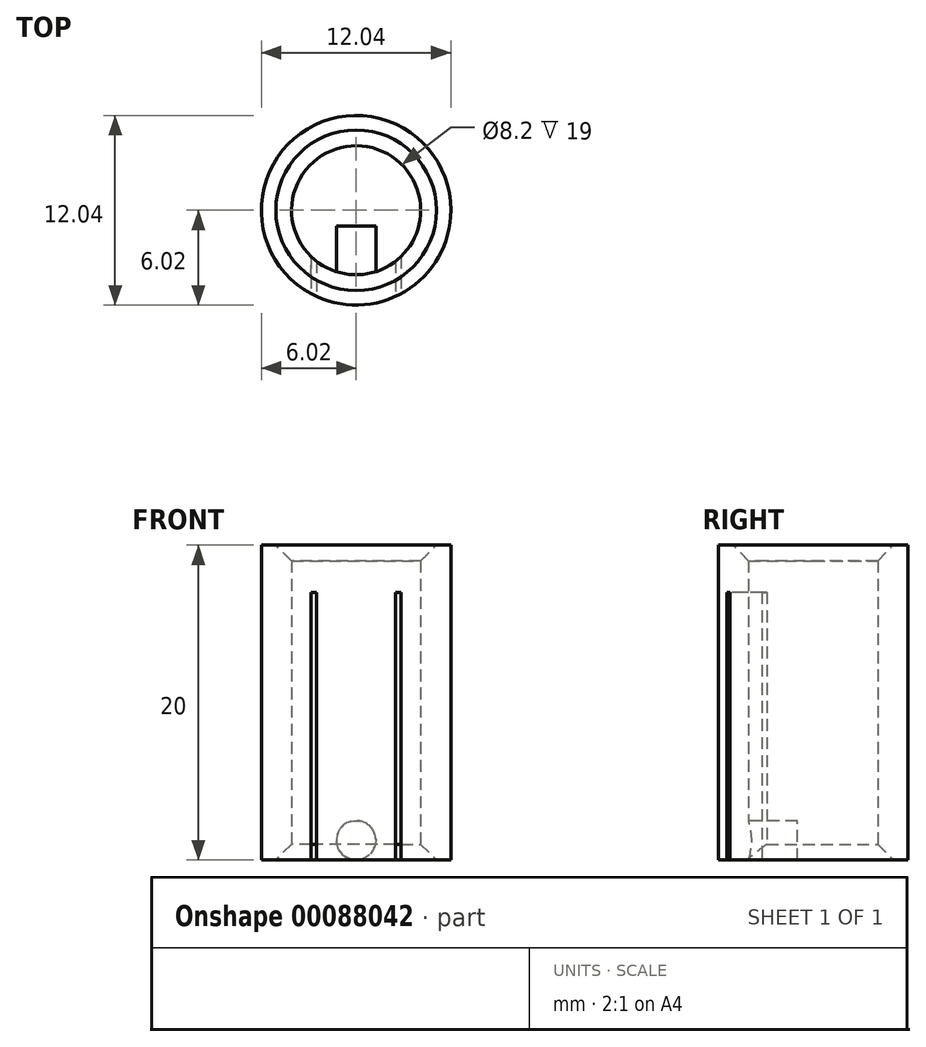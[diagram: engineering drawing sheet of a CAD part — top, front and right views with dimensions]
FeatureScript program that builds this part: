
annotation { "Feature Type Name" : "Feature", "Feature Type Description" : "" }
export const myFeature = defineFeature(function(context is Context, id is Id, definition is map)
    precondition{}
    {
        {
            var Q0;
            Q0=qCreatedBy(makeId("Top.planeOp"),FACE);
            var sketch = newSketch(context, id + "F0", { "sketchPlane" : qUnion([Q0])});
            skCircle(sketch, "E0", {"center": v(0, 0) * mm, "radius": 4.1 * mm});
            skCircle(sketch, "E1", {"center": v(0, 0) * mm, "radius": 6.02 * mm});
            skSolve(sketch);
        }
        {
            var Q0;
            Q0=makeQuery(id+"F0.imprint","IMPRINT",FACE,{"disambiguationData":[TD([[makeQuery(id+"F0.imprint","IMPRINT",EDGE,{"derivedFrom":sQuery(id+"F0.wireOp",EDGE,"E0")}),-1.0]])]});
            extrude(context, id + "F1", {"entities" : qUnion([Q0]), "depth" : 20 * mm});
        }
        {
            var Q0;
            Q0=qCreatedBy(makeId("Front.planeOp"),FACE);
            cPlane(context, id + "F2", {"entities" : qUnion([Q0]), "cplaneType" : CPlaneType.OFFSET, "offset" : 5 * mm, "width" : 150 * mm, "height" : 150 * mm});
        }
        {
            var Q0;
            Q0=qCreatedBy(id+"F2.planeOp",FACE);
            var sketch = newSketch(context, id + "F3", { "sketchPlane" : qUnion([Q0])});
            skCircle(sketch, "E2", {"center": v(0, 1.25) * mm, "radius": 1.25 * mm});
            skSolve(sketch);
        }
        {
            var Q0;
            Q0 = qSketchRegion(id + "F3", true);
            extrude(context, id + "F4", {"entities" : qUnion([Q0]), "operationType" : NewBodyOperationType.ADD, "oppositeDirection" : true, "depth" : 4 * mm});
        }
        {
            var Q0;
            Q0=qCreatedBy(id+"F2.planeOp",FACE);
            var sketch = newSketch(context, id + "F5", { "sketchPlane" : qUnion([Q0])});
            skLineSegment(sketch, "E3", {"start": v(-2.85, 0) * mm, "end": v(-2.85, 17) * mm});
            skLineSegment(sketch, "E4.0", {"start": v(-2.5, 0) * mm, "end": v(-2.5, 17) * mm});
            skLineSegment(sketch, "E5", {"start": v(-2.85, 17) * mm, "end": v(-2.5, 17) * mm});
            skLineSegment(sketch, "E6", {"start": v(-2.5, 0) * mm, "end": v(-2.85, 0) * mm});
            skLineSegment(sketch, "E7.MirrorCS", {"start": v(2.5, 0) * mm, "end": v(2.85, 0) * mm});
            skLineSegment(sketch, "E8.MirrorCS", {"start": v(2.85, 17) * mm, "end": v(2.5, 17) * mm});
            skLineSegment(sketch, "E9.MirrorCS", {"start": v(2.85, 0) * mm, "end": v(2.85, 17) * mm});
            skLineSegment(sketch, "E10.MirrorCS", {"start": v(2.5, 0) * mm, "end": v(2.5, 17) * mm});
            skSolve(sketch);
        }
        {
            var Q0;
            Q0 = qSketchRegion(id + "F5", true);
            extrude(context, id + "F6", {"entities" : qUnion([Q0]), "operationType" : NewBodyOperationType.REMOVE, "endBound" : BoundingType.SYMMETRIC, "oppositeDirection" : true, "depth" : 5 * mm});
        }
        {
            var Q0;
            Q0=makeQuery(id+"F1.opExtrude","CAP_EDGE",EDGE,{"disambiguationData":[OSD([sQuery(id+"F0.wireOp",EDGE,"E0")])],"isStart":false});
            var Q1;
            {var subQ0=sQuery(id+"F0.wireOp",EDGE,"E0");Q1=makeQuery(id+"F6.boolean.opBoolean","SPLIT",EDGE,{"disambiguationData":[TD([makeQuery(id+"F6.opExtrude","SWEPT_FACE",FACE,{"disambiguationData":[OSD([sQuery(id+"F5.wireOp",EDGE,"E3")])]})])],"derivedFrom":makeQuery(id+"F1.opExtrude","CAP_EDGE",EDGE,{"disambiguationData":[OSD([subQ0])],"isStart":true})});}
            chamfer(context, id + "F7", {"entities" : qUnion([Q0, Q1]), "width" : 1 * mm, "tangentPropagation" : true});
        }
    });
